# Revit family: Drain_Floor_Zurn-Z310-ThoroFlush
name_source: partatom
category: Plumbing Fixtures
units: mm (PartAtom-declared; Revit-internal decimal feet)

## family parameters
Always vertical = Yes
Cut with Voids When Loaded = No
Maintain Annotation Orientation = No
OmniClass Number = 23.45.55.21
OmniClass Title = Drains (Wastes)
Part Type = Normal
Room Calculation Point = No
Round Connector Dimension = Use Radius
Shared = No
Work Plane-Based = No

## types (12) — shared parameters
Approx. Weight (Lbs) = 20 "
Assembly Code = D2030300
CW Connection = No
Default Elevation = 20 "
Description = THOROFLUSH DRAIN
Grate Open Area = 18 "
HW Connection = No
Main Material = Cast Iron- Zurn- White A.R.E Coated- Interior
Manufacturer = Zurn Water, LLC
Manufacurer Brand = Zurn
Modified Date = 12/11/2025
Product Documentation Link = https://files.zurn.com
Product Page URL = https://www.zurn.com
Product data url = https://www.bimobject.com
URL = www.zurn.com
Vent Connection = No
WFU = 1
Waste Connection = Yes
zero-valued in all types: CWFU, HWFU

## per-type parameters (varying)
| type | Body Height_E | Connector Radius | Model | Pipe Size_A Inside Diameter | Pipe Size_A Inside Radius | Pipe Size_A Nominal Diameter | Pipe Size_A Nominal Radius | Pipe Size_A Outer Diameter | Pipe Size_A Outer Radius | Type Comments |
| ZB310-4 IP | 5.5 " | 2 " | ZB310 | 4.026 " | 2.013 " | 4 " | 2 " | 4.5 " | 2.25 " | ZB310 With 4 Inch Threaded Outlet |
| ZB310-4 NL | 4.625 " | 2 " | ZB310 | 4.026 " | 2.013 " | 4 " | 2 " | 4.5 " | 2.25 " | ZB310 With 4 Inch Neo-Loc Outlet |
| ZB310-2 IP | 5.5 " | 1 " | ZB310 | 2.067 " | 1.034 " | 2 " | 1 " | 2.375 " | 1.188 " | ZB310 With 2 Inch Threaded Outlet |
| ZB310-2 NL | 4.625 " | 1 " | ZB310 | 2.067 " | 1.034 " | 2 " | 1 " | 2.375 " | 1.188 " | ZB310 With 2 Inch Neo-Loc Outlet |
| ZB310-3 IP | 5.5 " | 1.5 " | ZB310 | 3.068 " | 1.534 " | 3 " | 1.5 " | 3.5 " | 1.75 " | ZB310 With 3 Inch Threaded Outlet |
| ZB310-3 NL | 4.625 " | 1.5 " | ZB310 | 3.068 " | 1.534 " | 3 " | 1.5 " | 3.5 " | 1.75 " | ZB310 With 3 Inch Neo-Loc Outlet |
| ZN310-4 IP | 5.5 " | 2 " | ZN310 | 4.026 " | 2.013 " | 4 " | 2 " | 4.5 " | 2.25 " | ZN310 With 4 Inch Threaded Outlet |
| ZN310-4NL | 4.625 " | 2 " | ZN310 | 4.026 " | 2.013 " | 4 " | 2 " | 4.5 " | 2.25 " | ZN310 With 4 Inch Neo-Loc Outlet |
| ZN310-2 IP | 5.5 " | 1 " | ZN310 | 2.067 " | 1.034 " | 2 " | 1 " | 2.375 " | 1.188 " | ZN310 With 2 Inch Threaded Outlet |
| ZN310-2 NL | 4.625 " | 1 " | ZN310 | 2.067 " | 1.034 " | 2 " | 1 " | 2.375 " | 1.188 " | ZN310 With 2 Inch Neo-Loc Outlet |
| ZN310-3 IP | 5.5 " | 1.5 " | ZN310 | 3.068 " | 1.534 " | 3 " | 1.5 " | 3.5 " | 1.75 " | ZN310 With 3 Inch Threaded Outlet |
| ZN310-3 NL | 4.625 " | 1.5 " | ZN310 | 3.068 " | 1.534 " | 3 " | 1.5 " | 3.5 " | 1.75 " | ZN310 With 3 Inch Neo-Loc Outlet |

## geometry (parser evidence)
native form markers: Blend x4, Sweep x4
no freeform markers — native parametric forms only
